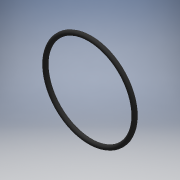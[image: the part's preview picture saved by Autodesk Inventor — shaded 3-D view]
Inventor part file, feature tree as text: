
AUTODESK INVENTOR PART (.ipt)
format: ipt  version: 2018 (Build 220112000, 112)  size: 118,272 bytes
history: native  units: mm
features: revolve x1, sketch x1
ambient origin geometry x8: Origin, YZ Plane, XZ Plane, XY Plane, X Axis, Y Axis, Z Axis, Center Point
bodies: Solid1 (feature_tree)
feature tree (2):
  revolve  "Revolution1"  [1 undecoded]
  sketch  "Sketch1"  dims[d0=3.5mm d1=35.0mm d2=90.0deg]
note: 1 required parameter value undecoded (feature->parameter linkage not recoverable at this tier; creation-order binding heuristic only, values carry confidence <= 0.55)
